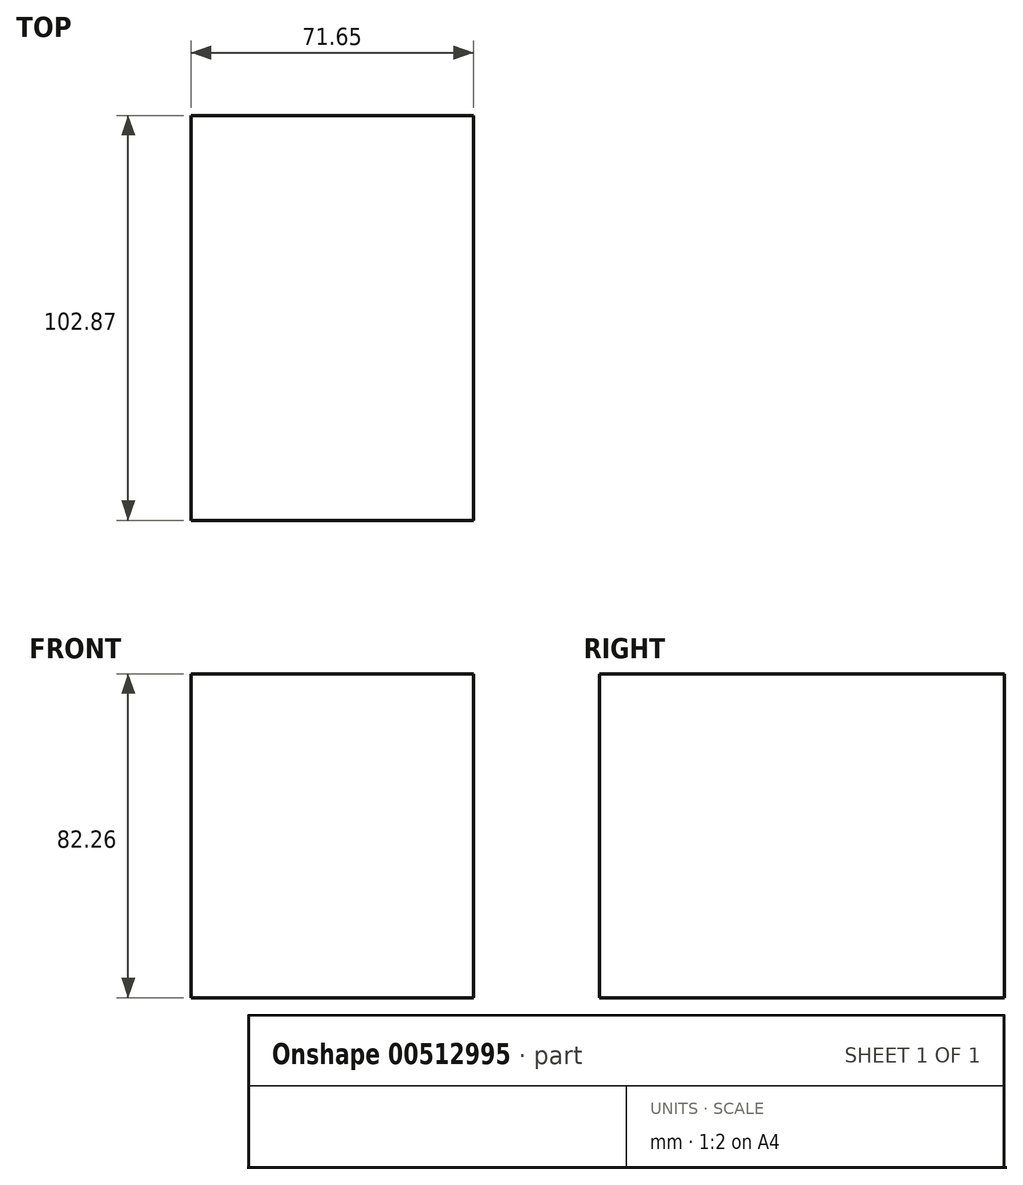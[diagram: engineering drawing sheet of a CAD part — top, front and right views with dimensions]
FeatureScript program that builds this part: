
annotation { "Feature Type Name" : "Feature", "Feature Type Description" : "" }
export const myFeature = defineFeature(function(context is Context, id is Id, definition is map)
    precondition{}
    {
        {
            var Q0;
            Q0=qCreatedBy(makeId("Front.planeOp"),FACE);
            var sketch = newSketch(context, id + "F0", { "sketchPlane" : qUnion([Q0])});
            skLineSegment(sketch, "E0.bottom", {"start": v(-27.66, 37.35) * mm, "end": v(44, 37.35) * mm});
            skLineSegment(sketch, "E0.top", {"start": v(-27.66, -44.9) * mm, "end": v(44, -44.9) * mm});
            skLineSegment(sketch, "E0.left", {"start": v(-27.66, 37.35) * mm, "end": v(-27.66, -44.9) * mm});
            skLineSegment(sketch, "E0.right", {"start": v(44, 37.35) * mm, "end": v(44, -44.9) * mm});
            skSolve(sketch);
        }
        {
            var Q0;
            Q0 = qSketchRegion(id + "F0", true);
            extrude(context, id + "F1", {"entities" : qUnion([Q0]), "depth" : 102.87 * mm});
        }
    });
